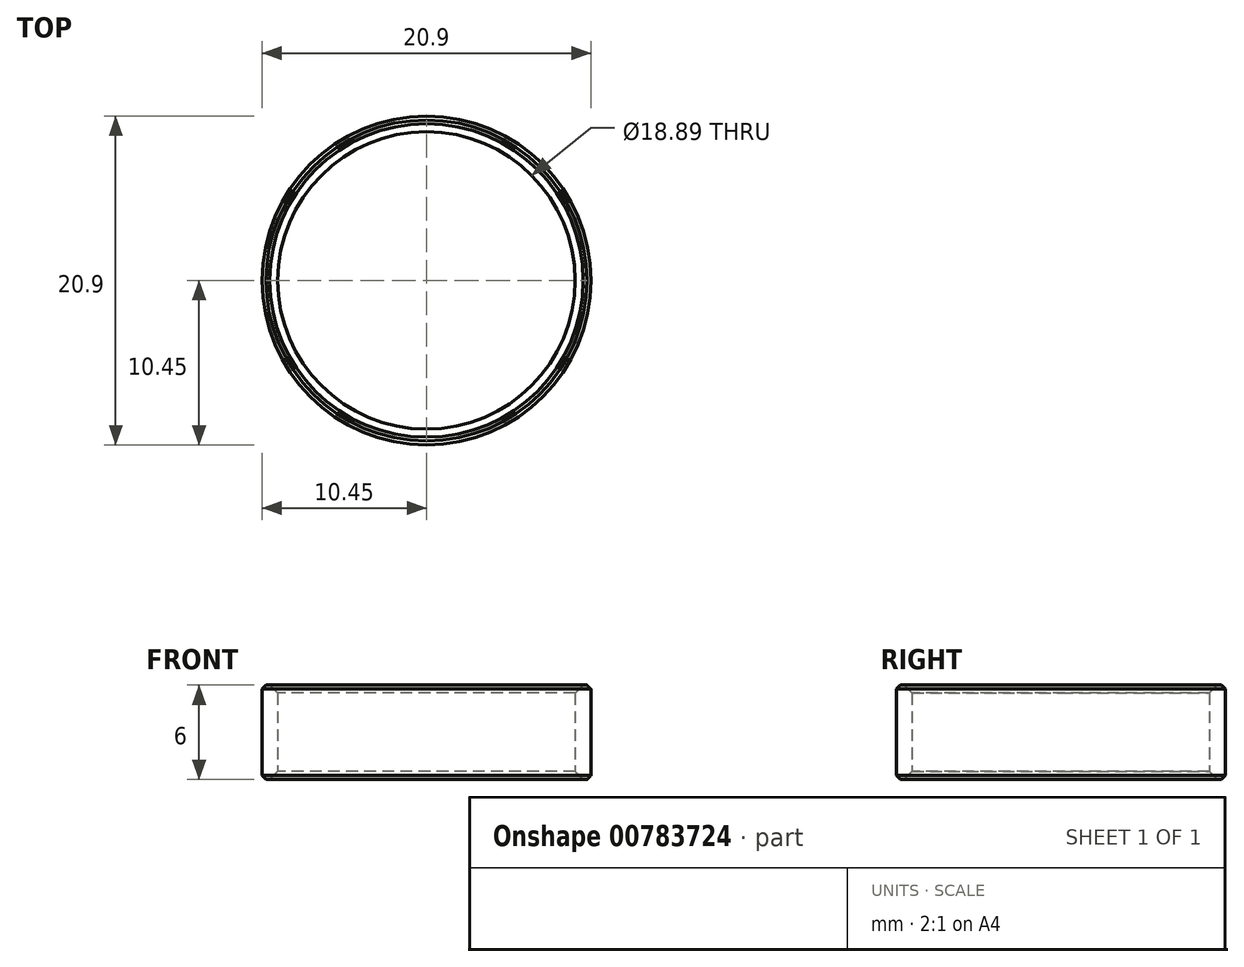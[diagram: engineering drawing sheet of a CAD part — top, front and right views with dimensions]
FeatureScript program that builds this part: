
annotation { "Feature Type Name" : "Feature", "Feature Type Description" : "" }
export const myFeature = defineFeature(function(context is Context, id is Id, definition is map)
    precondition{}
    {
        {
            var Q0;
            Q0=qCreatedBy(makeId("Top.planeOp"),FACE);
            var sketch = newSketch(context, id + "F0", { "sketchPlane" : qUnion([Q0])});
            skCircle(sketch, "E0", {"center": v(0, 0) * mm, "radius": 10.45 * mm});
            skCircle(sketch, "E1", {"center": v(0, 0) * mm, "radius": 9.45 * mm});
            skSolve(sketch);
        }
        {
            var Q0;
            Q0=makeQuery(id+"F0.imprint","IMPRINT",FACE,{"disambiguationData":[TD([[makeQuery(id+"F0.imprint","IMPRINT",EDGE,{"derivedFrom":sQuery(id+"F0.wireOp",EDGE,"E0")}),1.0]])]});
            extrude(context, id + "F1", {"entities" : qUnion([Q0]), "depth" : 6 * mm, "offsetDistance" : 25.4 * mm});
        }
        {
            var Q0;
            Q0=makeQuery(id+"F1.opExtrude","CAP_EDGE",EDGE,{"disambiguationData":[OSD([sQuery(id+"F0.wireOp",EDGE,"E1")])],"isStart":false});
            var Q1;
            Q1=makeQuery(id+"F1.opExtrude","CAP_EDGE",EDGE,{"disambiguationData":[OSD([sQuery(id+"F0.wireOp",EDGE,"E1")])],"isStart":true});
            chamfer(context, id + "F2", {"entities" : qUnion([Q0, Q1]), "width" : 0.5 * mm, "tangentPropagation" : true});
        }
        {
            var Q0;
            Q0=makeQuery(id+"F1.opExtrude","CAP_EDGE",EDGE,{"disambiguationData":[OSD([sQuery(id+"F0.wireOp",EDGE,"E0")])],"isStart":false});
            var Q1;
            Q1=makeQuery(id+"F1.opExtrude","CAP_EDGE",EDGE,{"disambiguationData":[OSD([sQuery(id+"F0.wireOp",EDGE,"E0")])],"isStart":true});
            chamfer(context, id + "F3", {"entities" : qUnion([Q0, Q1]), "width" : 0.25 * mm, "tangentPropagation" : true});
        }
    });
